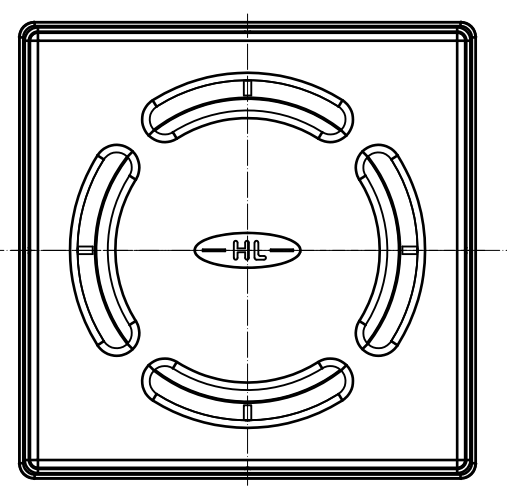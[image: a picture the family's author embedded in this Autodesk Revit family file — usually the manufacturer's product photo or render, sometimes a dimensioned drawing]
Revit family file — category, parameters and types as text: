
# Revit family: HL_Трап для балконов и террас_HL73.0
name_source: partatom
category: Instalační zařizovací předměty
revit_build: Autodesk Revit 2016 (Build: 20151007_0715(x64)
units: mm (PartAtom-declared; Revit-internal decimal feet)

## family parameters
Bod výpočtu místnosti = Ano
Kóta kulaté spojky = Použít průměr
Nadpis OmniClass = Deck Waste Water Drains
Ořezat dutým tvarem při načtení = Ne
Sdílené = Ne
Typ součásti = Normální
Vždy vertikální = Ano
Založené na pracovní rovině = Ne
Číslo OmniClass = 23.70.50.21.24.14

## types (1)
- HL_Трап для балконов и террас_HL73.0
    EAN = 9003076034420
    Klíčová poznámka = HL73.0
    Komentáře k typům = Трап для балконов и террас, универсальный, с вертикальным выпуском DN110 с гибкими "юбками" по диаметру, для любых безраструбных труб DN110.
    Model = HL73.0
    Popis = Трап для балконов и террас
    Připojení CW = Ne
    Připojení HW = Ne
    Připojení odpadu = Ano
    Připojení ventilace = Ne
    URL = http://www.hutterer-lechner.com
    Výrobce = HL Hutterer & Lechner GmbH
    ВЕС = 0,397 kg
    МАКСИМАЛЬНАЯ НАГРУЗКА КЛАССА = K3 - 300 kg
    МАТЕРИАЛ = PP / Edelstahl
    НАСАДКА = 121 x 121 mm
    НОМИНАЛЬНЫЙ ДИАМЕТР = 110 mm
    ПРОИЗВОДИТЕЛЬНОСТЬ = 1,1 l/s
    РАЗМЕР = DN110
    РЕШЁТКА = Edelstahl 115 x 115 mm

## geometry (parser evidence)
native form markers: Sweep x2
no freeform markers — native parametric forms only
